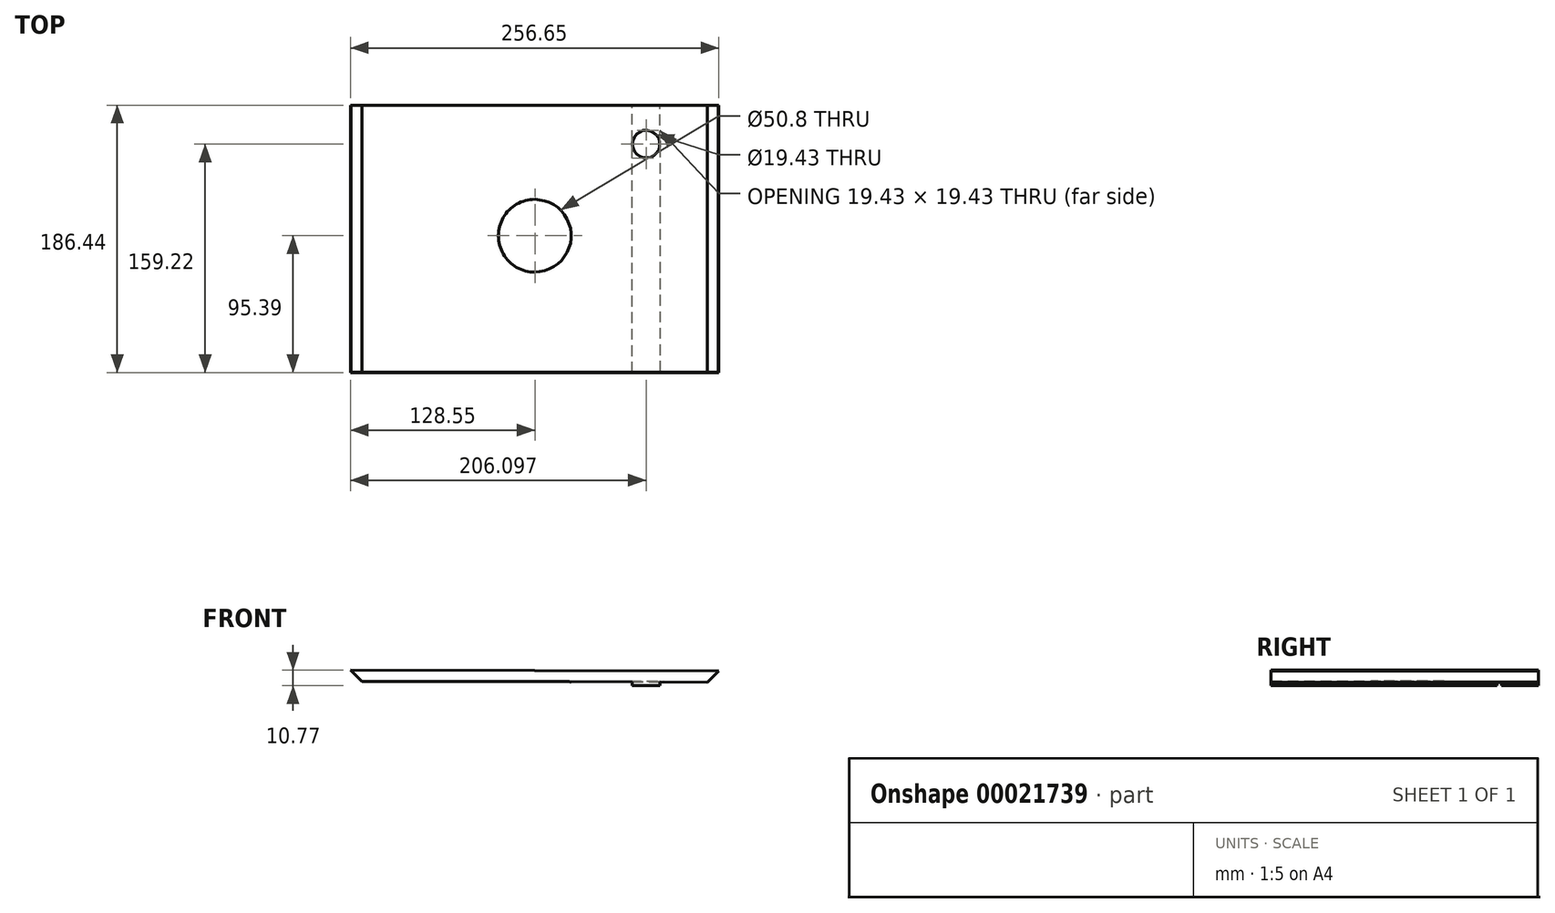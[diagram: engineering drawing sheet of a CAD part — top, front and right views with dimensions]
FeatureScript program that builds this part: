
annotation { "Feature Type Name" : "Feature", "Feature Type Description" : "" }
export const myFeature = defineFeature(function(context is Context, id is Id, definition is map)
    precondition{}
    {
        {
            var Q0;
            Q0=qCreatedBy(makeId("Front.planeOp"),FACE);
            var sketch = newSketch(context, id + "F0", { "sketchPlane" : qUnion([Q0])});
            skLineSegment(sketch, "E0", {"start": v(0, 0) * mm, "end": v(-120.65, 0) * mm});
            skLineSegment(sketch, "E1", {"start": v(-120.65, 0) * mm, "end": v(-128.55, 7.9) * mm});
            skLineSegment(sketch, "E2", {"start": v(-128.55, 7.9) * mm, "end": v(128.1, 7.46) * mm});
            skLineSegment(sketch, "E3", {"start": v(128.1, 7.46) * mm, "end": v(120.2, -0.45) * mm});
            skLineSegment(sketch, "E4", {"start": v(120.2, -0.45) * mm, "end": v(0, 0) * mm});
            skSolve(sketch);
        }
        {
            var Q0;
            Q0 = qSketchRegion(id + "F0", true);
            extrude(context, id + "F1", {"entities" : qUnion([Q0]), "depth" : 186.44 * mm});
        }
        {
            var Q0;
            Q0=makeQuery(id+"F1.opExtrude","SWEPT_FACE",FACE,{"disambiguationData":[OSD([sQuery(id+"F0.wireOp",EDGE,"E2")])]});
            shell(context, id + "F2", {"entities" : qUnion([Q0]), "thickness" : 0.25 * mm});
        }
        {
            var Q0;
            Q0=makeQuery(id+"F2.opShell","OFFSET_FACE",FACE,{"disambiguationData":[OSD([sQuery(id+"F0.wireOp",EDGE,"E0"),sQuery(id+"F0.wireOp",EDGE,"60ebadbe-ac62-4703-a873-5fbb37d307180.MirrorCS")])]});
            var sketch = newSketch(context, id + "F3", { "sketchPlane" : qUnion([Q0])});
            skCircle(sketch, "E5", {"center": v(0, -91.05) * mm, "radius": 25.4 * mm});
            skCircle(sketch, "E6", {"center": v(77.55, -27.22) * mm, "radius": 9.71 * mm});
            skSolve(sketch);
        }
        {
            var Q0;
            Q0=makeQuery(id+"F3.imprint","IMPRINT",FACE,{"disambiguationData":[TD([[makeQuery(id+"F3.imprint","IMPRINT",EDGE,{"derivedFrom":sQuery(id+"F3.wireOp",EDGE,"E6")}),1.0]])]});
            var Q1;
            {var subQ0=makeQuery(id+"F2.opShell","OFFSET_EDGE",EDGE,{"disambiguationData":[OSD([sQuery(id+"F0.wireOp",EDGE,"E0"),sQuery(id+"F0.wireOp",EDGE,"E4")])]});var subQ1=sQuery(id+"F3.wireOp",EDGE,"E5");var subQ3=makeQuery(id+"F3.imprint","INTERSECT",VERTEX,{"disambiguationData":[OD(0.0)],"derivedFrom":[subQ0,subQ1]});Q1=makeQuery(id+"F3.imprint","IMPRINT",FACE,{"disambiguationData":[TD([[makeQuery(id+"F3.imprint","IMPRINT",EDGE,{"disambiguationData":[TD([[subQ3,-1.0]])],"derivedFrom":subQ1}),1.0]])]});}
            var Q2;
            {var subQ0=makeQuery(id+"F2.opShell","OFFSET_EDGE",EDGE,{"disambiguationData":[OSD([sQuery(id+"F0.wireOp",EDGE,"E0"),sQuery(id+"F0.wireOp",EDGE,"E4")])]});var subQ1=sQuery(id+"F3.wireOp",EDGE,"E5");var subQ3=makeQuery(id+"F3.imprint","INTERSECT",VERTEX,{"disambiguationData":[OD(0.0)],"derivedFrom":[subQ0,subQ1]});Q2=makeQuery(id+"F3.imprint","IMPRINT",FACE,{"disambiguationData":[TD([[makeQuery(id+"F3.imprint","IMPRINT",EDGE,{"disambiguationData":[TD([[subQ3,1.0]])],"derivedFrom":subQ1}),1.0]])]});}
            var Q3;
            Q3=sQuery(id+"F3.wireOp",EDGE,"E5");
            extrude(context, id + "F4", {"entities" : qUnion([Q0, Q1, Q2]), "operationType" : NewBodyOperationType.REMOVE, "surfaceEntities" : qUnion([Q3]), "endBound" : BoundingType.THROUGH_ALL, "oppositeDirection" : true, "depth" : 25.4 * mm});
        }
        {
            var Q0;
            Q0=makeQuery(id+"F1.opExtrude","SWEPT_FACE",FACE,{"disambiguationData":[OSD([sQuery(id+"F0.wireOp",EDGE,"E4")])]});
            var sketch = newSketch(context, id + "F5", { "sketchPlane" : qUnion([Q0])});
            skLineSegment(sketch, "E7", {"start": v(87.26, 27.22) * mm, "end": v(87.26, 186.44) * mm});
            skLineSegment(sketch, "E8", {"start": v(67.83, 27.22) * mm, "end": v(67.83, 186.44) * mm});
            skLineSegment(sketch, "E9.bottom", {"start": v(87.26, 186.44) * mm, "end": v(67.93, 186.44) * mm});
            skLineSegment(sketch, "E9.top", {"start": v(87.26, 0) * mm, "end": v(67.93, 0) * mm});
            skLineSegment(sketch, "E9.left", {"start": v(87.26, 186.44) * mm, "end": v(87.26, 0) * mm});
            skLineSegment(sketch, "E9.right", {"start": v(67.93, 186.44) * mm, "end": v(67.93, 0) * mm});
            skCircle(sketch, "E10", {"center": v(77.55, 27.22) * mm, "radius": 9.85 * mm});
            skSolve(sketch);
        }
        {
            var Q0;
            {var subQ6=sQuery(id+"F5.wireOp",EDGE,"E9.top");Q0=makeQuery(id+"F5.imprint","IMPRINT",FACE,{"disambiguationData":[TD([[makeQuery(id+"F5.imprint","IMPRINT",EDGE,{"derivedFrom":subQ6}),-1.0]])]});}
            var Q1;
            {var subQ6=sQuery(id+"F5.wireOp",EDGE,"E9.bottom");Q1=makeQuery(id+"F5.imprint","IMPRINT",FACE,{"disambiguationData":[TD([[makeQuery(id+"F5.imprint","IMPRINT",EDGE,{"derivedFrom":subQ6}),1.0]])]});}
            extrude(context, id + "F6", {"entities" : qUnion([Q0, Q1]), "operationType" : NewBodyOperationType.ADD, "depth" : 2.54 * mm});
        }
    });
